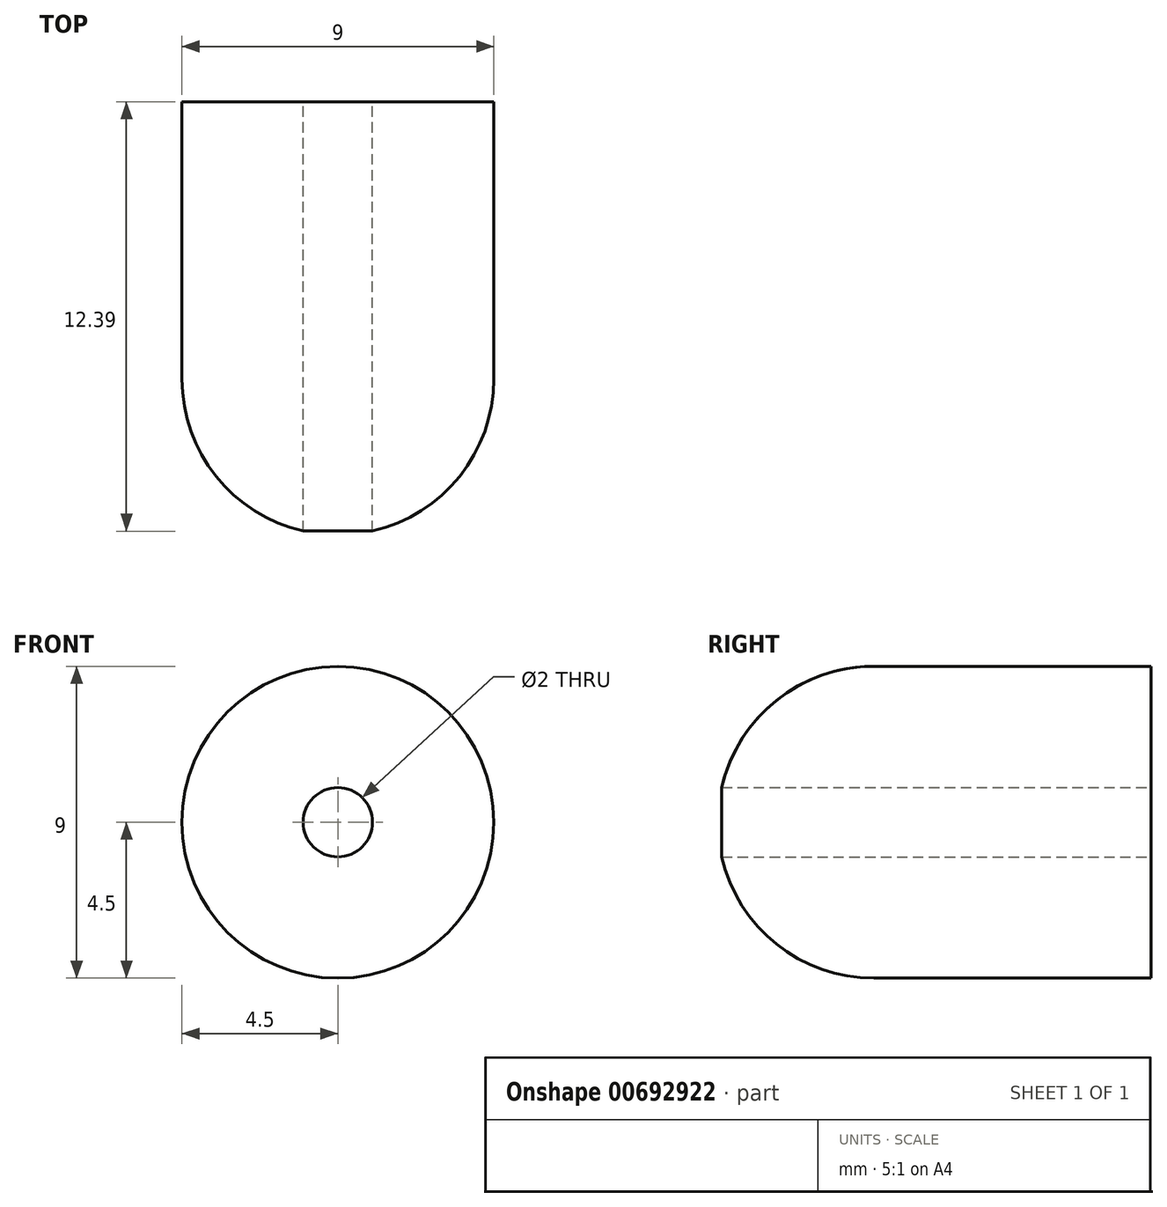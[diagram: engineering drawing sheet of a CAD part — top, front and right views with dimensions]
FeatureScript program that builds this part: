
annotation { "Feature Type Name" : "Feature", "Feature Type Description" : "" }
export const myFeature = defineFeature(function(context is Context, id is Id, definition is map)
    precondition{}
    {
        {
            var Q0;
            Q0=qCreatedBy(makeId("Front.planeOp"),FACE);
            var sketch = newSketch(context, id + "F0", { "sketchPlane" : qUnion([Q0])});
            skCircle(sketch, "E0", {"center": v(0, 0) * mm, "radius": 4.5 * mm});
            skSolve(sketch);
        }
        {
            var Q0;
            Q0=makeQuery(id+"F0.imprint","IMPRINT",FACE,{"disambiguationData":[TD([[makeQuery(id+"F0.imprint","IMPRINT",EDGE,{"derivedFrom":sQuery(id+"F0.wireOp",EDGE,"E0")}),1.0]])]});
            extrude(context, id + "F1", {"entities" : qUnion([Q0]), "depth" : 8 * mm, "offsetDistance" : 25 * mm});
        }
        {
            var Q0;
            Q0=qCreatedBy(makeId("Right.planeOp"),FACE);
            var sketch = newSketch(context, id + "F2", { "sketchPlane" : qUnion([Q0])});
            skLineSegment(sketch, "E1", {"start": v(-20.53, 0) * mm, "end": v(-32.13, 0) * mm});
            skArc(sketch, "E2", {"start": v(-8, 4.5) * mm, "mid": v(-11.18, 3.18) * mm, "end": v(-12.5, 0) * mm});
            skLineSegment(sketch, "E3", {"start": v(-8, 0) * mm, "end": v(-8, 4.5) * mm});
            skLineSegment(sketch, "E4", {"start": v(-8, 4.5) * mm, "end": v(-8, 0) * mm});
            skLineSegment(sketch, "E5", {"start": v(-8, 0) * mm, "end": v(-12.5, 0) * mm});
            skSolve(sketch);
        }
        {
            var Q0;
            Q0=makeQuery(id+"F2.imprint","IMPRINT",FACE,{"disambiguationData":[TD([[makeQuery(id+"F2.imprint","IMPRINT",EDGE,{"derivedFrom":sQuery(id+"F2.wireOp",EDGE,"E2")}),1.0]])]});
            var Q1;
            Q1=sQuery(id+"F2.wireOp",EDGE,"E1");
            revolve(context, id + "F3", {"operationType" : NewBodyOperationType.ADD, "entities" : qUnion([Q0]), "axis" : qUnion([Q1]), "revolveType" : RevolveType.FULL});
        }
        {
            var Q0;
            Q0=qCreatedBy(makeId("Front.planeOp"),FACE);
            var sketch = newSketch(context, id + "F4", { "sketchPlane" : qUnion([Q0])});
            skCircle(sketch, "E6", {"center": v(0, 0) * mm, "radius": 1 * mm});
            skSolve(sketch);
        }
        {
            var Q0;
            Q0 = qSketchRegion(id + "F4", true);
            extrude(context, id + "F5", {"entities" : qUnion([Q0]), "operationType" : NewBodyOperationType.REMOVE, "endBound" : BoundingType.THROUGH_ALL, "depth" : 25 * mm, "offsetDistance" : 25 * mm});
        }
    });
